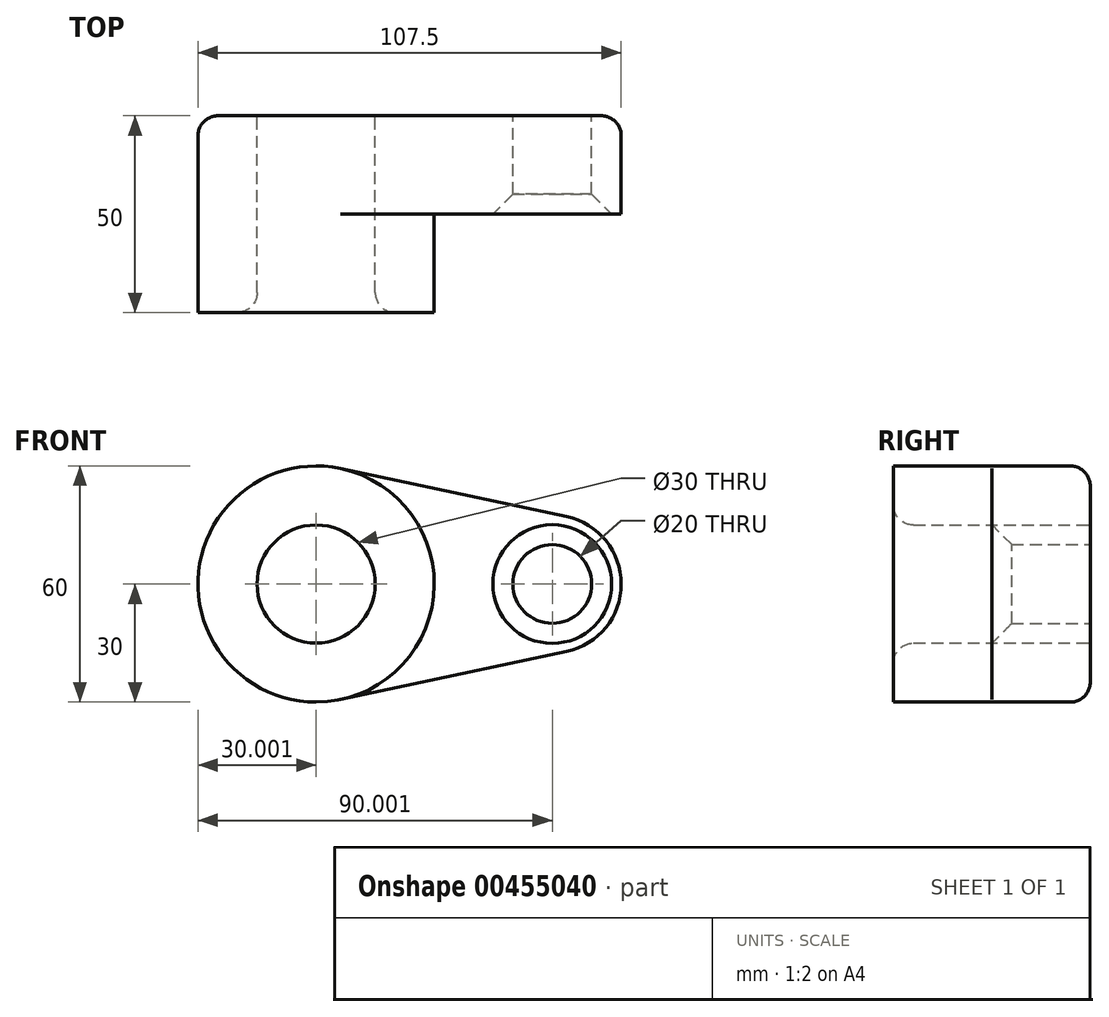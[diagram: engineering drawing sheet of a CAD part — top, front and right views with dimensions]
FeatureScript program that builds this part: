
annotation { "Feature Type Name" : "Feature", "Feature Type Description" : "" }
export const myFeature = defineFeature(function(context is Context, id is Id, definition is map)
    precondition{}
    {
        {
            var Q0;
            Q0=qCreatedBy(makeId("Front.planeOp"),FACE);
            var sketch = newSketch(context, id + "F0", { "sketchPlane" : qUnion([Q0])});
            skCircle(sketch, "E0", {"center": v(-55.1, 0) * mm, "radius": 30 * mm});
            skCircle(sketch, "E1", {"center": v(4.9, 0) * mm, "radius": 17.5 * mm});
            skLineSegment(sketch, "E2", {"start": v(-48.86, 29.34) * mm, "end": v(8.54, 17.12) * mm});
            skLineSegment(sketch, "E3", {"start": v(-48.86, -29.34) * mm, "end": v(8.54, -17.12) * mm});
            skCircle(sketch, "E4", {"center": v(-55.1, 0) * mm, "radius": 15 * mm});
            skCircle(sketch, "E5", {"center": v(4.9, 0) * mm, "radius": 10 * mm});
            skSolve(sketch);
        }
        {
            var Q0;
            Q0 = qSketchRegion(id + "F0", true);
            extrude(context, id + "F1", {"entities" : qUnion([Q0]), "depth" : 25 * mm});
        }
        {
            var Q0;
            Q0=makeQuery(id+"F0.imprint","IMPRINT",FACE,{"disambiguationData":[TD([[makeQuery(id+"F0.imprint","IMPRINT",EDGE,{"derivedFrom":sQuery(id+"F0.wireOp",EDGE,"E4")}),-1.0]])]});
            extrude(context, id + "F2", {"entities" : qUnion([Q0]), "operationType" : NewBodyOperationType.ADD, "depth" : 50 * mm});
        }
        {
            var Q0;
            Q0=makeQuery(id+"F2.opExtrude","CAP_EDGE",EDGE,{"disambiguationData":[OSD([sQuery(id+"F0.wireOp",EDGE,"E4")])],"isStart":false});
            var Q1;
            Q1=makeQuery(id+"F1.opExtrude","CAP_EDGE",EDGE,{"disambiguationData":[OSD([sQuery(id+"F0.wireOp",EDGE,"E3")])],"isStart":true});
            fillet(context, id + "F3", {"entities" : qUnion([Q0, Q1]), "radius" : 5.08 * mm, "tangentPropagation" : true, "allowEdgeOverflow" : false});
        }
        {
            var Q0;
            Q0=makeQuery(id+"F3.opFillet","BLEND_FACE",FACE,{"disambiguationData":[OSD([sQuery(id+"F0.wireOp",EDGE,"E4")])]});
            var Q1;
            Q1=makeQuery(id+"F1.opExtrude","CAP_EDGE",EDGE,{"disambiguationData":[OSD([sQuery(id+"F0.wireOp",EDGE,"E5")])],"isStart":false});
            chamfer(context, id + "F4", {"entities" : qUnion([Q0, Q1]), "width" : 5.08 * mm, "tangentPropagation" : true});
        }
    });
